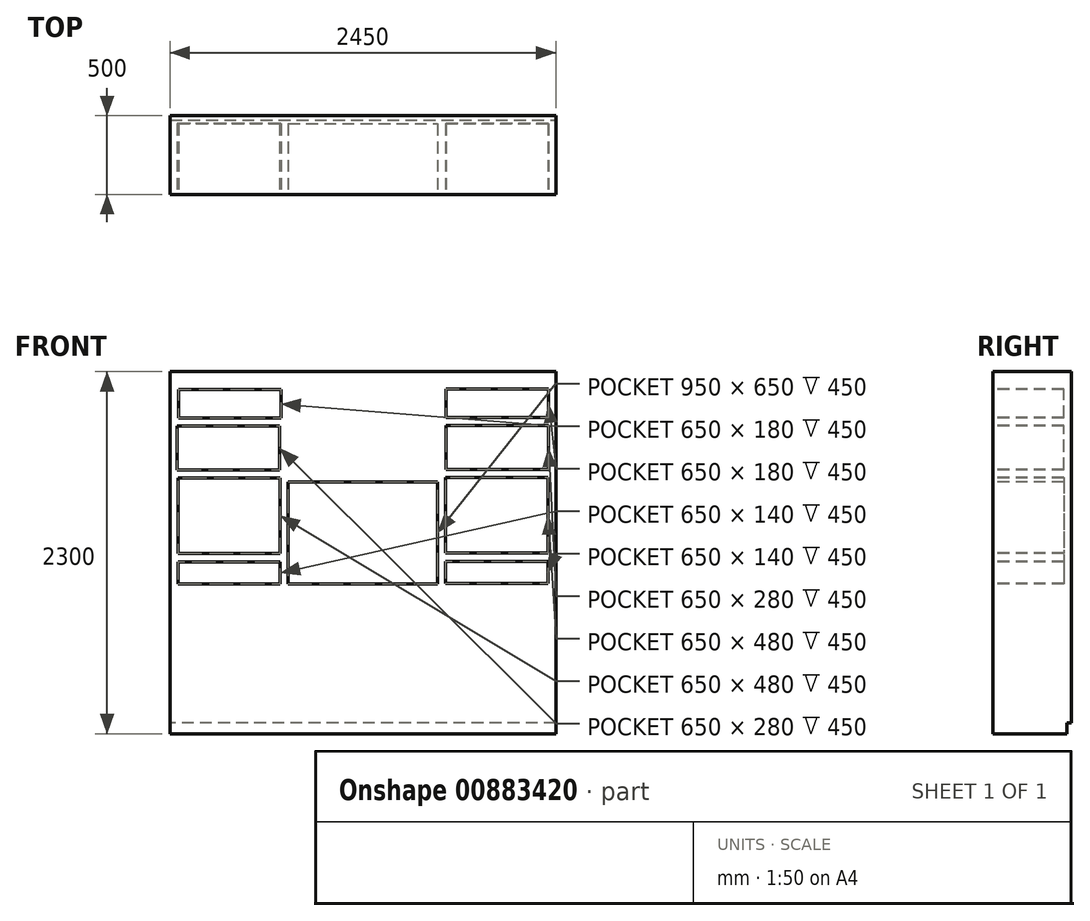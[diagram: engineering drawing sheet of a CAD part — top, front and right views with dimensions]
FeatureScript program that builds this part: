
annotation { "Feature Type Name" : "Feature", "Feature Type Description" : "" }
export const myFeature = defineFeature(function(context is Context, id is Id, definition is map)
    precondition{}
    {
        {
            var Q0;
            Q0=qCreatedBy(makeId("Front.planeOp"),FACE);
            var sketch = newSketch(context, id + "F0", { "sketchPlane" : qUnion([Q0])});
            skLineSegment(sketch, "E0.bottom", {"start": v(-1225, 1150) * mm, "end": v(1225, 1150) * mm});
            skLineSegment(sketch, "E0.top", {"start": v(-1225, -1150) * mm, "end": v(1225, -1150) * mm});
            skLineSegment(sketch, "E0.left", {"start": v(-1225, 1150) * mm, "end": v(-1225, -1150) * mm});
            skLineSegment(sketch, "E0.right", {"start": v(1225, 1150) * mm, "end": v(1225, -1150) * mm});
            skSolve(sketch);
        }
        {
            var Q0;
            Q0=makeQuery(id+"F0.imprint","IMPRINT",FACE,{"disambiguationData":[TD([[makeQuery(id+"F0.imprint","IMPRINT",EDGE,{"derivedFrom":sQuery(id+"F0.wireOp",EDGE,"E0.bottom")}),-1.0]])]});
            var Q1;
            Q1 = qSketchRegion(id + "F0", true);
            extrude(context, id + "F1", {"entities" : qUnion([Q0, Q1]), "depth" : 500 * mm, "offsetDistance" : 25 * mm});
        }
        {
            var Q0;
            Q0=makeQuery(id+"F1.opExtrude","CAP_FACE",FACE,{"disambiguationData":[OSD([sQuery(id+"F0.wireOp",EDGE,"E0.bottom"),sQuery(id+"F0.wireOp",EDGE,"E0.top"),sQuery(id+"F0.wireOp",EDGE,"E0.left"),sQuery(id+"F0.wireOp",EDGE,"E0.right")])],"isStart":true});
            var sketch = newSketch(context, id + "F2", { "sketchPlane" : qUnion([Q0])});
            skLineSegment(sketch, "E1.bottom", {"start": v(-1225, -1150) * mm, "end": v(1225, -1150) * mm});
            skLineSegment(sketch, "E1.top", {"start": v(-1225, -1079.88) * mm, "end": v(1225, -1079.88) * mm});
            skLineSegment(sketch, "E1.left", {"start": v(-1225, -1150) * mm, "end": v(-1225, -1079.88) * mm});
            skLineSegment(sketch, "E1.right", {"start": v(1225, -1150) * mm, "end": v(1225, -1079.88) * mm});
            skSolve(sketch);
        }
        {
            var Q0;
            Q0=makeQuery(id+"F2.imprint","IMPRINT",FACE,{"disambiguationData":[TD([[makeQuery(id+"F2.imprint","IMPRINT",EDGE,{"derivedFrom":sQuery(id+"F2.wireOp",EDGE,"E1.bottom")}),-1.0]])]});
            extrude(context, id + "F3", {"entities" : qUnion([Q0]), "operationType" : NewBodyOperationType.REMOVE, "oppositeDirection" : true, "depth" : 28 * mm, "offsetDistance" : 25 * mm});
        }
        {
            var Q0;
            Q0=makeQuery(id+"F1.opExtrude","CAP_FACE",FACE,{"disambiguationData":[OSD([sQuery(id+"F0.wireOp",EDGE,"E0.bottom"),sQuery(id+"F0.wireOp",EDGE,"E0.top"),sQuery(id+"F0.wireOp",EDGE,"E0.left"),sQuery(id+"F0.wireOp",EDGE,"E0.right")])],"isStart":false});
            var sketch = newSketch(context, id + "F4", { "sketchPlane" : qUnion([Q0])});
            skLineSegment(sketch, "E2.bottom", {"start": v(-475, 450) * mm, "end": v(475, 450) * mm});
            skLineSegment(sketch, "E2.top", {"start": v(-475, -200) * mm, "end": v(475, -200) * mm});
            skLineSegment(sketch, "E2.left", {"start": v(-475, 450) * mm, "end": v(-475, -200) * mm});
            skLineSegment(sketch, "E2.right", {"start": v(475, 450) * mm, "end": v(475, -200) * mm});
            skSolve(sketch);
        }
        {
            var Q0;
            Q0=makeQuery(id+"F4.imprint","IMPRINT",FACE,{"disambiguationData":[TD([[makeQuery(id+"F4.imprint","IMPRINT",EDGE,{"derivedFrom":sQuery(id+"F4.wireOp",EDGE,"E2.bottom")}),-1.0]])]});
            extrude(context, id + "F5", {"entities" : qUnion([Q0]), "operationType" : NewBodyOperationType.REMOVE, "oppositeDirection" : true, "depth" : 450 * mm, "offsetDistance" : 25 * mm});
        }
        {
            var Q0;
            Q0=makeQuery(id+"F1.opExtrude","CAP_FACE",FACE,{"disambiguationData":[OSD([sQuery(id+"F0.wireOp",EDGE,"E0.bottom"),sQuery(id+"F0.wireOp",EDGE,"E0.top"),sQuery(id+"F0.wireOp",EDGE,"E0.left"),sQuery(id+"F0.wireOp",EDGE,"E0.right")])],"isStart":false});
            var sketch = newSketch(context, id + "F6", { "sketchPlane" : qUnion([Q0])});
            skLineSegment(sketch, "E3.bottom", {"start": v(-520.85, 855.12) * mm, "end": v(-1170.85, 855.12) * mm});
            skLineSegment(sketch, "E3.top", {"start": v(-520.85, 1035.12) * mm, "end": v(-1170.85, 1035.12) * mm});
            skLineSegment(sketch, "E3.left", {"start": v(-520.85, 855.12) * mm, "end": v(-520.85, 1035.12) * mm});
            skLineSegment(sketch, "E3.right", {"start": v(-1170.85, 855.12) * mm, "end": v(-1170.85, 1035.12) * mm});
            skPoint(sketch, "E3.middle", {"position": v(-845.85, 945.12) * mm});
            skLineSegment(sketch, "E4.bottom", {"start": v(-528.75, 525.12) * mm, "end": v(-1178.75, 525.12) * mm});
            skLineSegment(sketch, "E4.top", {"start": v(-528.75, 805.12) * mm, "end": v(-1178.75, 805.12) * mm});
            skLineSegment(sketch, "E4.left", {"start": v(-528.75, 525.12) * mm, "end": v(-528.75, 805.12) * mm});
            skLineSegment(sketch, "E4.right", {"start": v(-1178.75, 525.12) * mm, "end": v(-1178.75, 805.12) * mm});
            skPoint(sketch, "E4.middle", {"position": v(-853.75, 665.12) * mm});
            skPoint(sketch, "E5", {"position": v(-853.75, 525.12) * mm});
            skLineSegment(sketch, "E6.bottom", {"start": v(-1175, 475.12) * mm, "end": v(-525, 475.12) * mm});
            skLineSegment(sketch, "E6.top", {"start": v(-1175, -4.88) * mm, "end": v(-525, -4.88) * mm});
            skLineSegment(sketch, "E6.left", {"start": v(-1175, 475.12) * mm, "end": v(-1175, -4.88) * mm});
            skLineSegment(sketch, "E6.right", {"start": v(-525, 475.12) * mm, "end": v(-525, -4.88) * mm});
            skPoint(sketch, "E6.middle", {"position": v(-850, 235.12) * mm});
            skLineSegment(sketch, "E7.bottom", {"start": v(524.65, 478.82) * mm, "end": v(1174.65, 478.82) * mm});
            skLineSegment(sketch, "E7.top", {"start": v(524.65, -1.18) * mm, "end": v(1174.65, -1.18) * mm});
            skLineSegment(sketch, "E7.left", {"start": v(524.65, 478.82) * mm, "end": v(524.65, -1.18) * mm});
            skLineSegment(sketch, "E7.right", {"start": v(1174.65, 478.82) * mm, "end": v(1174.65, -1.18) * mm});
            skPoint(sketch, "E7.middle", {"position": v(849.65, 238.82) * mm});
            skLineSegment(sketch, "E8.bottom", {"start": v(1178.6, 528.82) * mm, "end": v(528.6, 528.82) * mm});
            skLineSegment(sketch, "E8.top", {"start": v(1178.6, 808.82) * mm, "end": v(528.6, 808.82) * mm});
            skLineSegment(sketch, "E8.left", {"start": v(1178.6, 528.82) * mm, "end": v(1178.6, 808.82) * mm});
            skLineSegment(sketch, "E8.right", {"start": v(528.6, 528.82) * mm, "end": v(528.6, 808.82) * mm});
            skPoint(sketch, "E8.middle", {"position": v(853.6, 668.82) * mm});
            skLineSegment(sketch, "E9.bottom", {"start": v(1178.6, 858.82) * mm, "end": v(528.6, 858.82) * mm});
            skLineSegment(sketch, "E9.top", {"start": v(1178.6, 1038.82) * mm, "end": v(528.6, 1038.82) * mm});
            skLineSegment(sketch, "E9.left", {"start": v(1178.6, 858.82) * mm, "end": v(1178.6, 1038.82) * mm});
            skLineSegment(sketch, "E9.right", {"start": v(528.6, 858.82) * mm, "end": v(528.6, 1038.82) * mm});
            skPoint(sketch, "E9.middle", {"position": v(853.6, 948.82) * mm});
            skLineSegment(sketch, "E10.bottom", {"start": v(-1175, -59.88) * mm, "end": v(-525, -59.88) * mm});
            skLineSegment(sketch, "E10.top", {"start": v(-1175, -199.88) * mm, "end": v(-525, -199.88) * mm});
            skLineSegment(sketch, "E10.left", {"start": v(-1175, -59.88) * mm, "end": v(-1175, -199.88) * mm});
            skLineSegment(sketch, "E10.right", {"start": v(-525, -59.88) * mm, "end": v(-525, -199.88) * mm});
            skPoint(sketch, "E10.middle", {"position": v(-850, -129.88) * mm});
            skLineSegment(sketch, "E11.bottom", {"start": v(524.95, -56.18) * mm, "end": v(1174.95, -56.18) * mm});
            skLineSegment(sketch, "E11.top", {"start": v(524.95, -196.18) * mm, "end": v(1174.95, -196.18) * mm});
            skLineSegment(sketch, "E11.left", {"start": v(524.95, -56.18) * mm, "end": v(524.95, -196.18) * mm});
            skLineSegment(sketch, "E11.right", {"start": v(1174.95, -56.18) * mm, "end": v(1174.95, -196.18) * mm});
            skPoint(sketch, "E11.middle", {"position": v(849.95, -126.18) * mm});
            skSolve(sketch);
        }
        {
            var Q0;
            Q0 = qSketchRegion(id + "F6", true);
            extrude(context, id + "F7", {"entities" : qUnion([Q0]), "operationType" : NewBodyOperationType.REMOVE, "oppositeDirection" : true, "depth" : 450 * mm, "offsetDistance" : 25 * mm});
        }
    });
